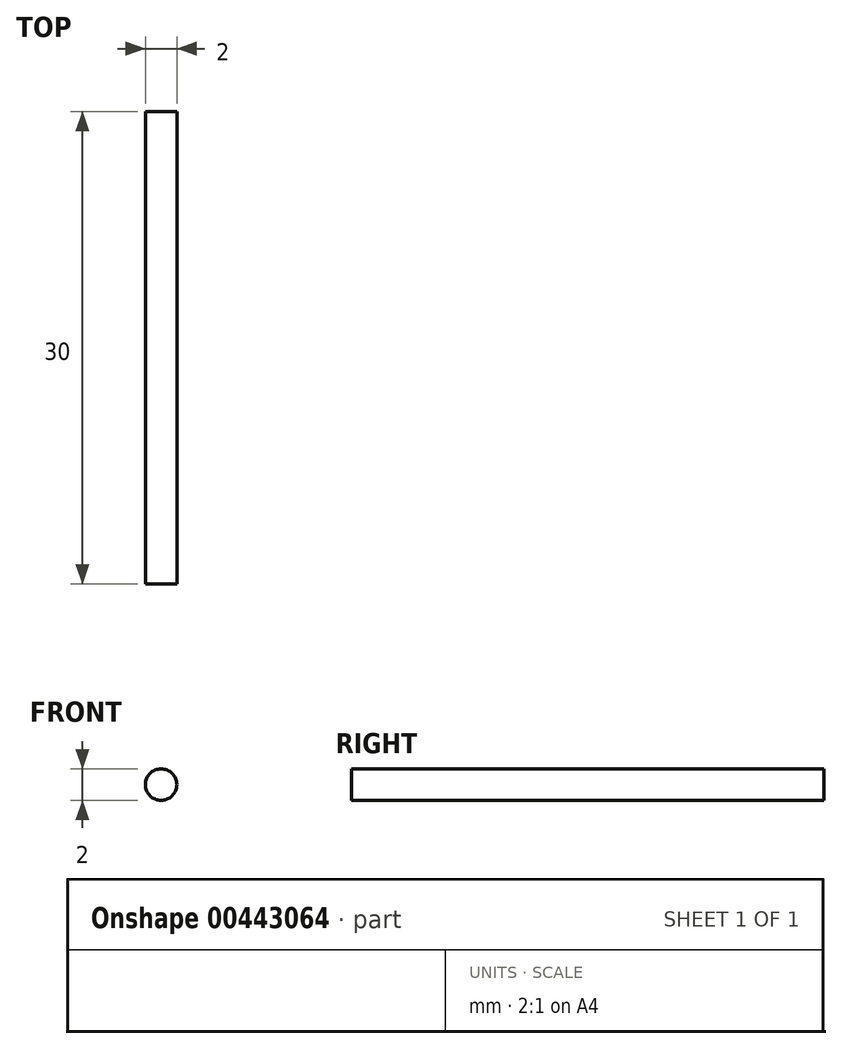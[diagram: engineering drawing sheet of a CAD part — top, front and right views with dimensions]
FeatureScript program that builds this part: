
annotation { "Feature Type Name" : "Feature", "Feature Type Description" : "" }
export const myFeature = defineFeature(function(context is Context, id is Id, definition is map)
    precondition{}
    {
        {
            var Q0;
            Q0=qCreatedBy(makeId("Front.planeOp"),FACE);
            var sketch = newSketch(context, id + "F0", { "sketchPlane" : qUnion([Q0])});
            skCircle(sketch, "E0", {"center": v(0, 0) * mm, "radius": 1 * mm});
            skSolve(sketch);
        }
        {
            var Q0;
            Q0=makeQuery(id+"F0.imprint","IMPRINT",FACE,{"disambiguationData":[TD([[makeQuery(id+"F0.imprint","IMPRINT",EDGE,{"derivedFrom":sQuery(id+"F0.wireOp",EDGE,"E0")}),1.0]])]});
            extrude(context, id + "F1", {"entities" : qUnion([Q0]), "depth" : 30 * mm});
        }
    });
